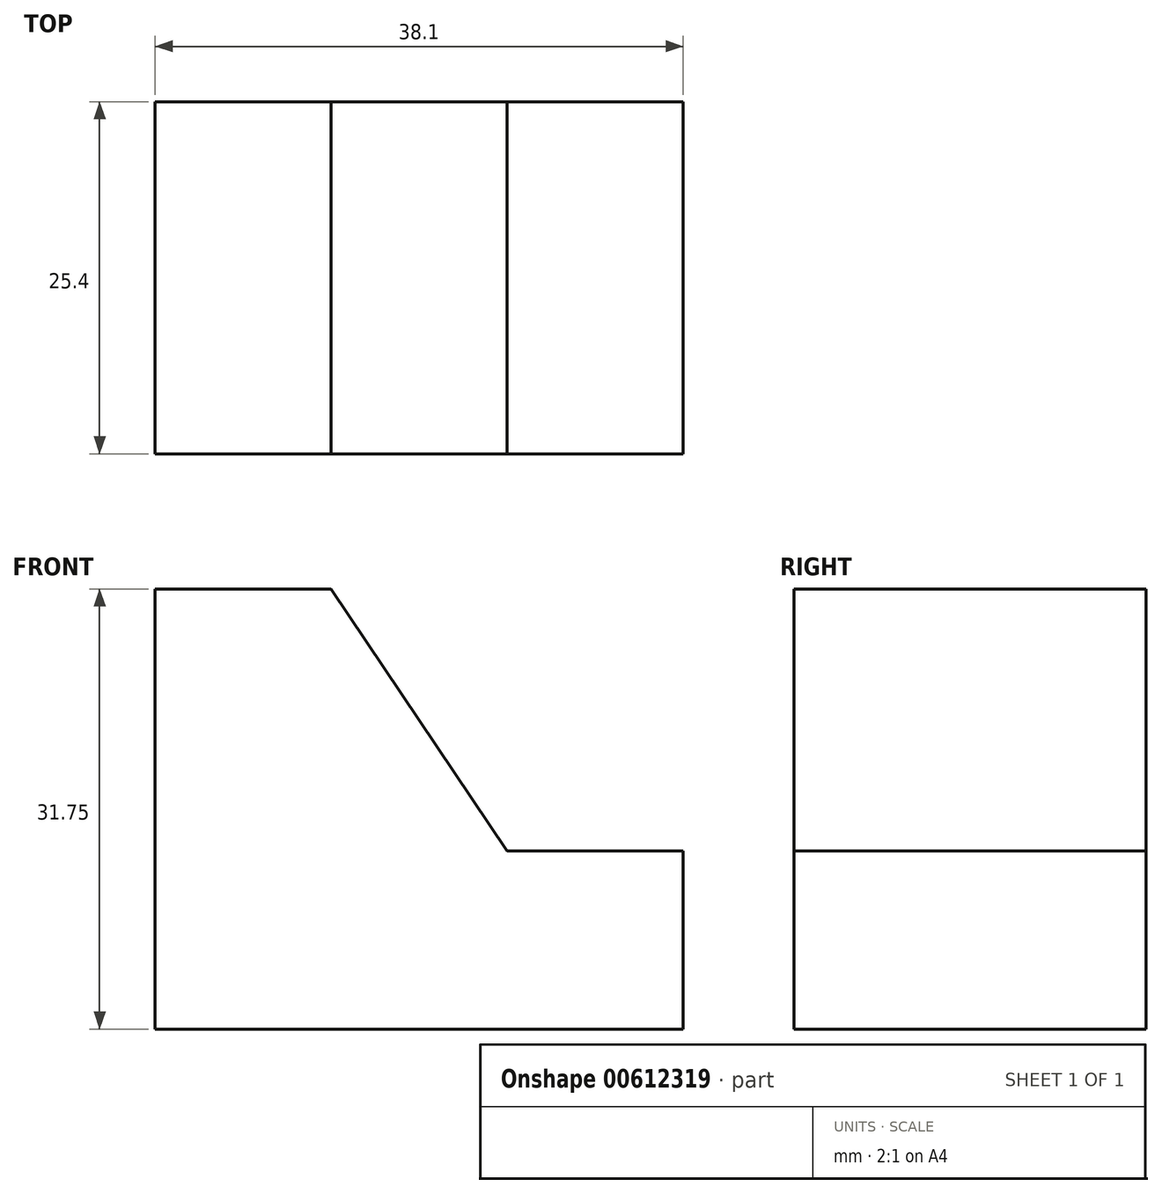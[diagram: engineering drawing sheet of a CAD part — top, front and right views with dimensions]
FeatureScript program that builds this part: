
annotation { "Feature Type Name" : "Feature", "Feature Type Description" : "" }
export const myFeature = defineFeature(function(context is Context, id is Id, definition is map)
    precondition{}
    {
        {
            var Q0;
            Q0=qCreatedBy(makeId("Front.planeOp"),FACE);
            var sketch = newSketch(context, id + "F0", { "sketchPlane" : qUnion([Q0])});
            skLineSegment(sketch, "E0", {"start": v(0, 0) * mm, "end": v(0, 31.75) * mm});
            skLineSegment(sketch, "E1", {"start": v(0, 31.75) * mm, "end": v(38.1, 31.75) * mm});
            skLineSegment(sketch, "E2", {"start": v(38.1, 31.75) * mm, "end": v(38.1, 0) * mm});
            skLineSegment(sketch, "E3", {"start": v(38.1, 0) * mm, "end": v(0, 0) * mm});
            skSolve(sketch);
        }
        {
            var Q0;
            Q0=makeQuery(id+"F0.imprint","IMPRINT",FACE,{"disambiguationData":[TD([[makeQuery(id+"F0.imprint","IMPRINT",EDGE,{"derivedFrom":sQuery(id+"F0.wireOp",EDGE,"E0")}),-1.0]])]});
            extrude(context, id + "F1", {"entities" : qUnion([Q0]), "depth" : 25.4 * mm});
        }
        {
            var Q0;
            Q0=makeQuery(id+"F1.opExtrude","CAP_FACE",FACE,{"disambiguationData":[OSD([sQuery(id+"F0.wireOp",EDGE,"E0"),sQuery(id+"F0.wireOp",EDGE,"E1"),sQuery(id+"F0.wireOp",EDGE,"E2"),sQuery(id+"F0.wireOp",EDGE,"E3")])],"isStart":false});
            var sketch = newSketch(context, id + "F2", { "sketchPlane" : qUnion([Q0])});
            skLineSegment(sketch, "E4", {"start": v(12.7, 31.75) * mm, "end": v(25.4, 12.84) * mm});
            skLineSegment(sketch, "E5", {"start": v(25.4, 12.84) * mm, "end": v(38.1, 12.84) * mm});
            skSolve(sketch);
        }
        {
            var Q0;
            Q0=qSketchRegion(id+"F2",true);
            var Q1;
            {var subQ0=sQuery(id+"F2.wireOp",EDGE,"E4");Q1=makeQuery(id+"F2.imprint","IMPRINT",FACE,{"disambiguationData":[TD([[makeQuery(id+"F2.imprint","IMPRINT",EDGE,{"derivedFrom":subQ0}),1.0]])]});}
            extrude(context, id + "F3", {"entities" : qUnion([Q0, Q1]), "operationType" : NewBodyOperationType.REMOVE, "oppositeDirection" : true, "depth" : 25.4 * mm});
        }
    });
